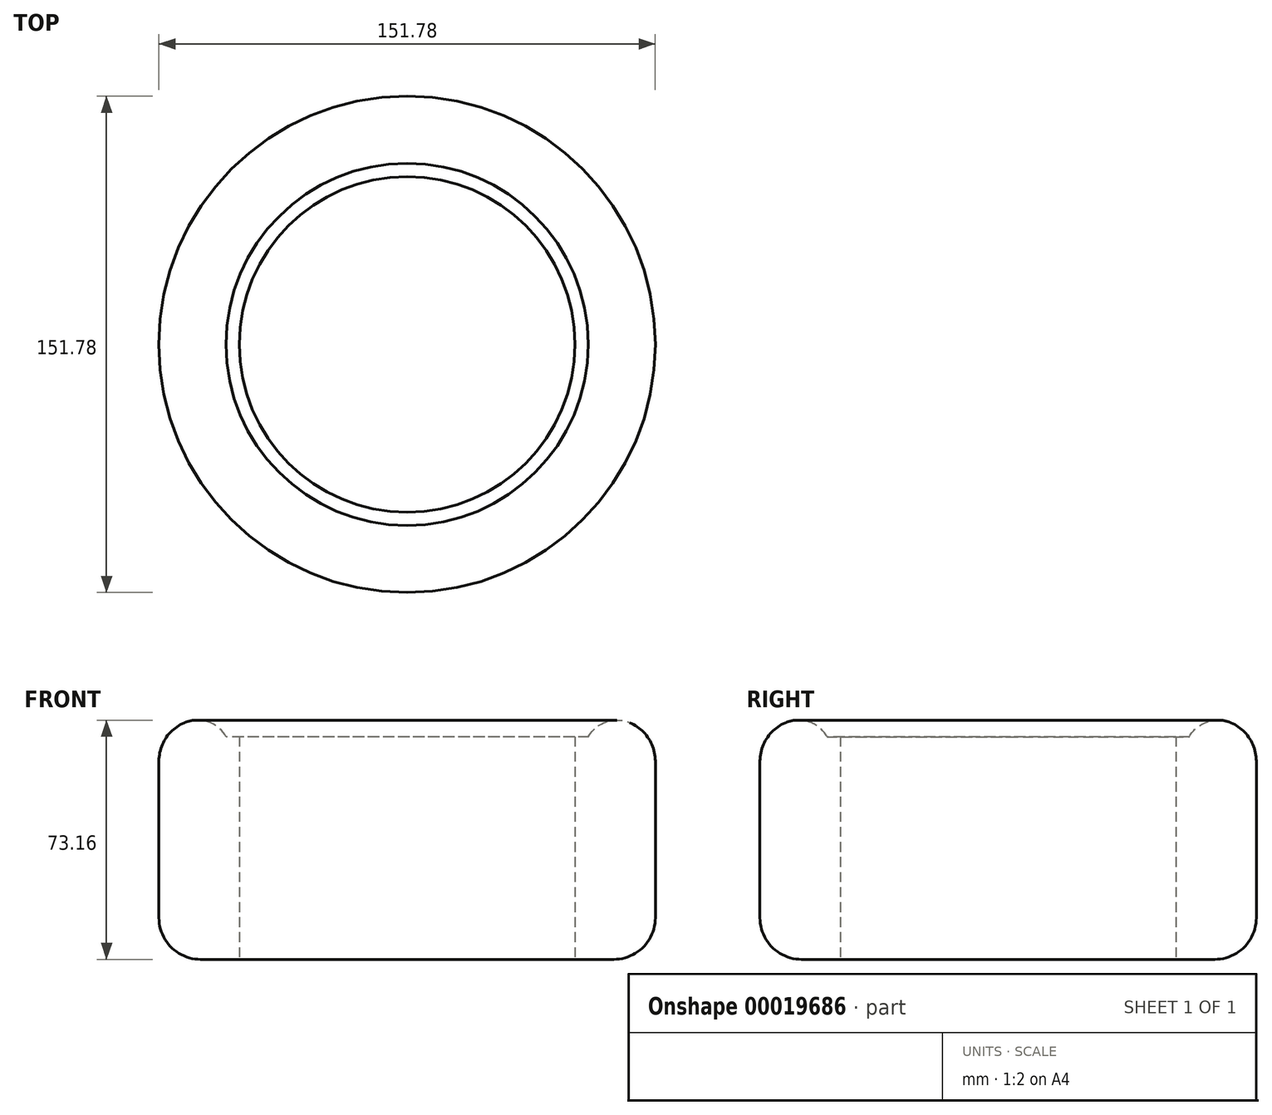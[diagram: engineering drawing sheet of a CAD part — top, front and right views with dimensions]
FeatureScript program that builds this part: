
annotation { "Feature Type Name" : "Feature", "Feature Type Description" : "" }
export const myFeature = defineFeature(function(context is Context, id is Id, definition is map)
    precondition{}
    {
        {
            var Q0;
            Q0=qCreatedBy(makeId("Top.planeOp"),FACE);
            var sketch = newSketch(context, id + "F0", { "sketchPlane" : qUnion([Q0])});
            skCircle(sketch, "E0", {"center": v(0, 0) * mm, "radius": 75.9 * mm});
            skCircle(sketch, "E1", {"center": v(0, 0) * mm, "radius": 55.38 * mm});
            skSolve(sketch);
        }
        {
            var Q0;
            Q0=makeQuery(id+"F0.imprint","IMPRINT",FACE,{"disambiguationData":[TD([[makeQuery(id+"F0.imprint","IMPRINT",EDGE,{"derivedFrom":sQuery(id+"F0.wireOp",EDGE,"E0")}),1.0]])]});
            extrude(context, id + "F1", {"entities" : qUnion([Q0]), "depth" : 73.36 * mm});
        }
        {
            var Q0;
            Q0=makeQuery(id+"F1.opExtrude","CAP_EDGE",EDGE,{"disambiguationData":[OSD([sQuery(id+"F0.wireOp",EDGE,"E0")])],"isStart":false});
            fillet(context, id + "F2", {"entities" : qUnion([Q0]), "radius" : 12.7 * mm, "tangentPropagation" : true, "allowEdgeOverflow" : false});
        }
        {
            var Q0;
            Q0=qCreatedBy(makeId("Top.planeOp"),FACE);
            var sketch = newSketch(context, id + "F3", { "sketchPlane" : qUnion([Q0])});
            skCircle(sketch, "E2", {"center": v(0, 0) * mm, "radius": 55.44 * mm});
            skCircle(sketch, "E3", {"center": v(0, 0) * mm, "radius": 51.33 * mm});
            skSolve(sketch);
        }
        {
            var Q0;
            Q0=makeQuery(id+"F3.imprint","IMPRINT",FACE,{"disambiguationData":[TD([[makeQuery(id+"F3.imprint","IMPRINT",EDGE,{"derivedFrom":sQuery(id+"F3.wireOp",EDGE,"E2")}),1.0]])]});
            extrude(context, id + "F4", {"entities" : qUnion([Q0]), "operationType" : NewBodyOperationType.ADD, "depth" : 68.1 * mm});
        }
        {
            var Q0;
            Q0=makeQuery(id+"F1.opExtrude","CAP_EDGE",EDGE,{"disambiguationData":[OSD([sQuery(id+"F0.wireOp",EDGE,"E1")])],"isStart":false});
            fillet(context, id + "F5", {"entities" : qUnion([Q0]), "radius" : 10.16 * mm, "tangentPropagation" : true, "allowEdgeOverflow" : false});
        }
        {
            var Q0;
            Q0=makeQuery(id+"F1.opExtrude","CAP_EDGE",EDGE,{"disambiguationData":[OSD([sQuery(id+"F0.wireOp",EDGE,"E0")])],"isStart":true});
            fillet(context, id + "F6", {"entities" : qUnion([Q0]), "radius" : 12.7 * mm, "tangentPropagation" : true, "allowEdgeOverflow" : false});
        }
    });
